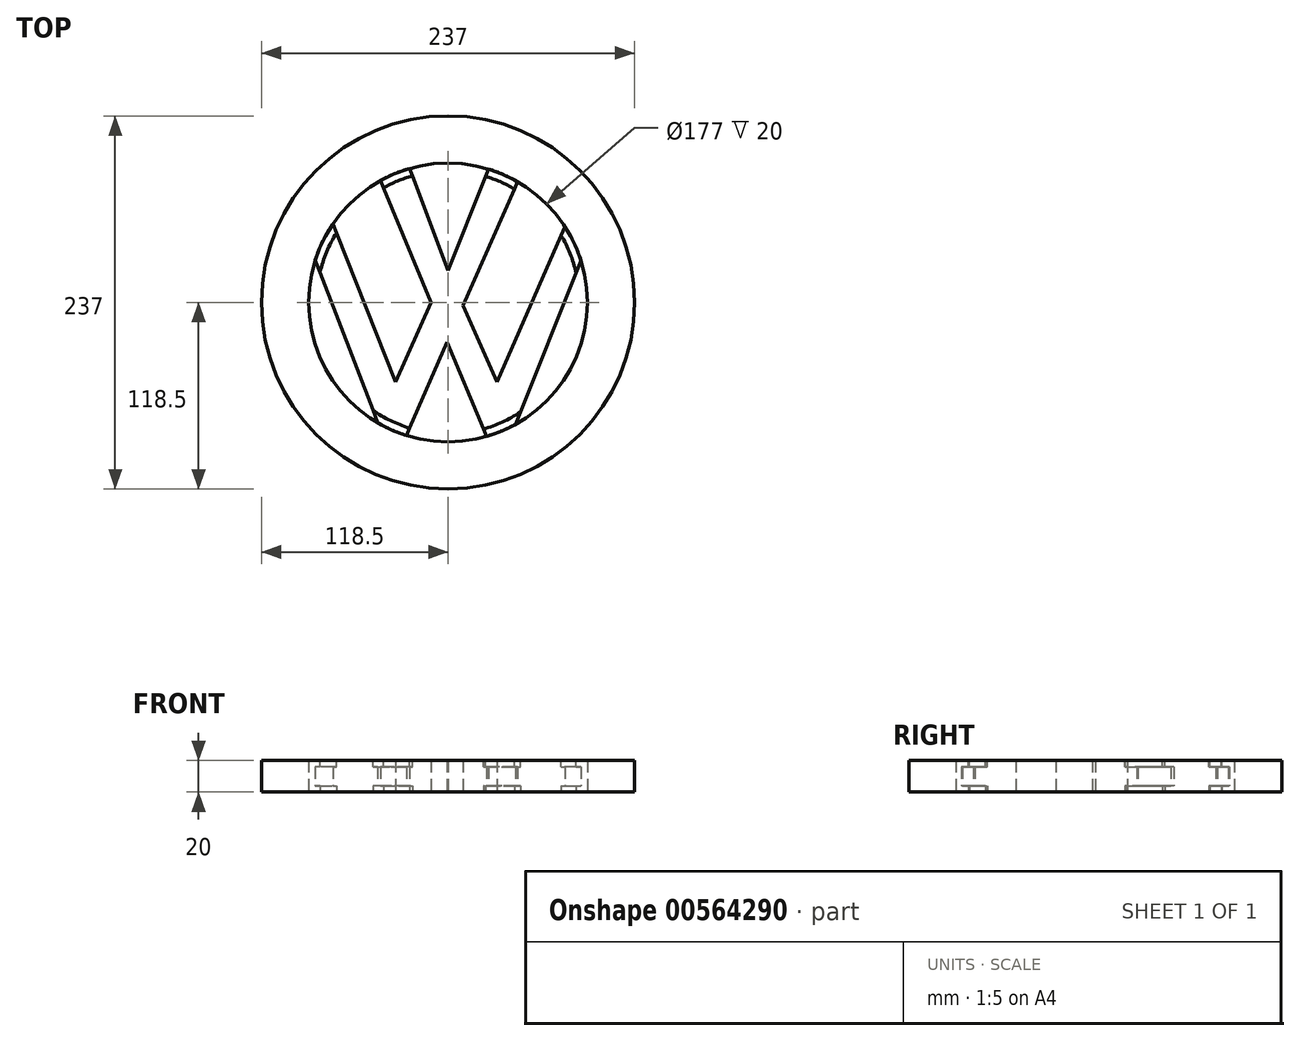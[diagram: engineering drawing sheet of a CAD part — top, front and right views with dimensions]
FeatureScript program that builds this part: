
annotation { "Feature Type Name" : "Feature", "Feature Type Description" : "" }
export const myFeature = defineFeature(function(context is Context, id is Id, definition is map)
    precondition{}
    {
        {
            var Q0;
            Q0=qCreatedBy(makeId("Top.planeOp"),FACE);
            var sketch = newSketch(context, id + "F0", { "sketchPlane" : qUnion([Q0])});
            skCircle(sketch, "E0", {"center": v(0, 0) * mm, "radius": 118.5 * mm});
            skCircle(sketch, "E1", {"center": v(0, 0) * mm, "radius": 88.5 * mm});
            skLineSegment(sketch, "E2", {"start": v(-24.48, 85.05) * mm, "end": v(0, 20.32) * mm});
            skLineSegment(sketch, "E3", {"start": v(0, 20.32) * mm, "end": v(25.75, 84.67) * mm});
            skLineSegment(sketch, "E4", {"start": v(-42.95, 77.38) * mm, "end": v(24.31, -85.1) * mm});
            skLineSegment(sketch, "E5", {"start": v(44.1, 76.73) * mm, "end": v(-26.48, -84.44) * mm});
            skLineSegment(sketch, "E6", {"start": v(-10.91, 0) * mm, "end": v(-44.77, -76.34) * mm});
            skLineSegment(sketch, "E7", {"start": v(8.81, 0) * mm, "end": v(42.8, -77.46) * mm});
            skPoint(sketch, "E7.startSnap0", {"position": v(8.81, -3.86) * mm});
            skLineSegment(sketch, "E8", {"start": v(-44.77, -76.34) * mm, "end": v(-84.3, 26.96) * mm});
            skLineSegment(sketch, "E9", {"start": v(-73.11, 49.87) * mm, "end": v(-33.34, -50.57) * mm});
            skLineSegment(sketch, "E10", {"start": v(42.8, -77.46) * mm, "end": v(84.46, 26.44) * mm});
            skLineSegment(sketch, "E11", {"start": v(31, -50.57) * mm, "end": v(74.25, 48.16) * mm});
            skSolve(sketch);
        }
        {
            var Q0;
            Q0=qSketchRegion(id+"F0",true);
            extrude(context, id + "F1", {"entities" : qUnion([Q0]), "depth" : 20 * mm, "offsetDistance" : 25 * mm});
        }
        {
            var Q0;
            {var subQ0=sQuery(id+"F0.wireOp",EDGE,"E8");Q0=makeQuery(id+"F0.imprint","IMPRINT",FACE,{"disambiguationData":[TD([[makeQuery(id+"F0.imprint","IMPRINT",EDGE,{"derivedFrom":subQ0}),-1.0]])]});}
            var Q1;
            {var subQ3=sQuery(id+"F0.wireOp",EDGE,"E4");var subQ5=sQuery(id+"F0.wireOp",EDGE,"E6");var subQ7=makeQuery(id+"F0.imprint","INTERSECT",VERTEX,{"derivedFrom":[subQ3,subQ5]});Q1=makeQuery(id+"F0.imprint","IMPRINT",FACE,{"disambiguationData":[TD([[makeQuery(id+"F0.imprint","IMPRINT",EDGE,{"disambiguationData":[TD([[subQ7,-1.0]])],"derivedFrom":subQ3}),-1.0]])]});}
            var Q2;
            {var subQ4=sQuery(id+"F0.wireOp",EDGE,"E2");Q2=makeQuery(id+"F0.imprint","IMPRINT",FACE,{"disambiguationData":[TD([[makeQuery(id+"F0.imprint","IMPRINT",EDGE,{"derivedFrom":subQ4}),-1.0]])]});}
            var Q3;
            {var subQ4=sQuery(id+"F0.wireOp",EDGE,"E4");var subQ6=sQuery(id+"F0.wireOp",EDGE,"E1");var subQ7=makeQuery(id+"F0.imprint","INTERSECT",VERTEX,{"disambiguationData":[OD(1.0)],"derivedFrom":[subQ6,subQ4]});Q3=makeQuery(id+"F0.imprint","IMPRINT",FACE,{"disambiguationData":[TD([[makeQuery(id+"F0.imprint","IMPRINT",EDGE,{"disambiguationData":[TD([[subQ7,1.0]])],"derivedFrom":subQ4}),1.0]])]});}
            var Q4;
            {var subQ0=sQuery(id+"F0.wireOp",EDGE,"E10");Q4=makeQuery(id+"F0.imprint","IMPRINT",FACE,{"disambiguationData":[TD([[makeQuery(id+"F0.imprint","IMPRINT",EDGE,{"derivedFrom":subQ0}),1.0]])]});}
            extrude(context, id + "F2", {"entities" : qUnion([Q0, Q1, Q2, Q3, Q4]), "operationType" : NewBodyOperationType.ADD, "depth" : 20 * mm, "offsetDistance" : 25 * mm});
        }
        {
            var Q0;
            {var subQ0=sQuery(id+"F0.wireOp",EDGE,"E1");Q0=makeQuery(id+"F2.boolean.opBoolean","MERGE",FACE,{"derivedFrom":[makeQuery(id+"F1.opExtrude","CAP_FACE",FACE,{"disambiguationData":[OSD([sQuery(id+"F0.wireOp",EDGE,"E0"),subQ0])],"isStart":false}),makeQuery(id+"F2.opExtrude","CAP_FACE",FACE,{"disambiguationData":[OSD([subQ0,sQuery(id+"F0.wireOp",EDGE,"E2"),sQuery(id+"F0.wireOp",EDGE,"E3"),sQuery(id+"F0.wireOp",EDGE,"E4"),sQuery(id+"F0.wireOp",EDGE,"E5"),sQuery(id+"F0.wireOp",EDGE,"E6"),sQuery(id+"F0.wireOp",EDGE,"E7"),sQuery(id+"F0.wireOp",EDGE,"E8"),sQuery(id+"F0.wireOp",EDGE,"E9"),sQuery(id+"F0.wireOp",EDGE,"E10"),sQuery(id+"F0.wireOp",EDGE,"E11")])],"isStart":false})]});}
            var sketch = newSketch(context, id + "F3", { "sketchPlane" : qUnion([Q0])});
            skCircle(sketch, "E12", {"center": v(0, 0) * mm, "radius": 88.5 * mm});
            skCircle(sketch, "E13", {"center": v(0, 0) * mm, "radius": 83.5 * mm});
            skLineSegment(sketch, "E14.bottom", {"start": v(-12.16, 3) * mm, "end": v(10.13, 3) * mm});
            skLineSegment(sketch, "E14.top", {"start": v(-12.16, -3) * mm, "end": v(10.13, -3) * mm});
            skLineSegment(sketch, "E14.left", {"start": v(-12.16, 3) * mm, "end": v(-12.16, -3) * mm});
            skLineSegment(sketch, "E14.right", {"start": v(10.13, 3) * mm, "end": v(10.13, -3) * mm});
            skSolve(sketch);
        }
        {
            var Q0;
            {var subQ0=sQuery(id+"F3.wireOp",EDGE,"E12");var subQ4=makeQuery(id+"F2.opExtrude","CAP_EDGE",EDGE,{"disambiguationData":[OSD([sQuery(id+"F0.wireOp",EDGE,"E10")])],"isStart":false});var subQ5=makeQuery(id+"F3.imprint","INTERSECT",VERTEX,{"disambiguationData":[OD(0.0)],"derivedFrom":[subQ4,subQ0]});Q0=makeQuery(id+"F3.imprint","IMPRINT",FACE,{"disambiguationData":[TD([[makeQuery(id+"F3.imprint","IMPRINT",EDGE,{"disambiguationData":[TD([[subQ5,-1.0]])],"derivedFrom":subQ4}),1.0]])]});}
            var Q1;
            {var subQ0=sQuery(id+"F3.wireOp",EDGE,"E12");var subQ4=makeQuery(id+"F2.opExtrude","CAP_EDGE",EDGE,{"disambiguationData":[OSD([sQuery(id+"F0.wireOp",EDGE,"E8")])],"isStart":false});var subQ5=makeQuery(id+"F3.imprint","INTERSECT",VERTEX,{"disambiguationData":[OD(0.0)],"derivedFrom":[subQ4,subQ0]});Q1=makeQuery(id+"F3.imprint","IMPRINT",FACE,{"disambiguationData":[TD([[makeQuery(id+"F3.imprint","IMPRINT",EDGE,{"disambiguationData":[TD([[subQ5,-1.0]])],"derivedFrom":subQ4}),-1.0]])]});}
            var Q2;
            {var subQ0=sQuery(id+"F3.wireOp",EDGE,"E12");var subQ1=makeQuery(id+"F2.opExtrude","CAP_EDGE",EDGE,{"disambiguationData":[OSD([sQuery(id+"F0.wireOp",EDGE,"E8")])],"isStart":false});var subQ2=makeQuery(id+"F3.imprint","INTERSECT",VERTEX,{"disambiguationData":[OD(1.0)],"derivedFrom":[subQ1,subQ0]});Q2=makeQuery(id+"F3.imprint","IMPRINT",FACE,{"disambiguationData":[TD([[makeQuery(id+"F3.imprint","IMPRINT",EDGE,{"disambiguationData":[TD([[subQ2,1.0]])],"derivedFrom":subQ0}),1.0]])]});}
            var Q3;
            {var subQ0=sQuery(id+"F3.wireOp",EDGE,"E12");var subQ1=makeQuery(id+"F2.opExtrude","CAP_EDGE",EDGE,{"disambiguationData":[OSD([sQuery(id+"F0.wireOp",EDGE,"E2")])],"isStart":false});var subQ2=makeQuery(id+"F3.imprint","INTERSECT",VERTEX,{"derivedFrom":[subQ1,subQ0]});Q3=makeQuery(id+"F3.imprint","IMPRINT",FACE,{"disambiguationData":[TD([[makeQuery(id+"F3.imprint","IMPRINT",EDGE,{"disambiguationData":[TD([[subQ2,-1.0]])],"derivedFrom":subQ1}),-1.0]])]});}
            var Q4;
            {var subQ0=sQuery(id+"F3.wireOp",EDGE,"E12");var subQ1=makeQuery(id+"F2.opExtrude","CAP_EDGE",EDGE,{"disambiguationData":[OSD([sQuery(id+"F0.wireOp",EDGE,"E3")])],"isStart":false});var subQ2=makeQuery(id+"F3.imprint","INTERSECT",VERTEX,{"derivedFrom":[subQ1,subQ0]});Q4=makeQuery(id+"F3.imprint","IMPRINT",FACE,{"disambiguationData":[TD([[makeQuery(id+"F3.imprint","IMPRINT",EDGE,{"disambiguationData":[TD([[subQ2,1.0]])],"derivedFrom":subQ1}),-1.0]])]});}
            var Q5;
            {var subQ0=sQuery(id+"F3.wireOp",EDGE,"E12");var subQ1=makeQuery(id+"F2.opExtrude","CAP_EDGE",EDGE,{"disambiguationData":[OSD([sQuery(id+"F0.wireOp",EDGE,"E10")])],"isStart":false});var subQ2=makeQuery(id+"F3.imprint","INTERSECT",VERTEX,{"disambiguationData":[OD(1.0)],"derivedFrom":[subQ1,subQ0]});Q5=makeQuery(id+"F3.imprint","IMPRINT",FACE,{"disambiguationData":[TD([[makeQuery(id+"F3.imprint","IMPRINT",EDGE,{"disambiguationData":[TD([[subQ2,-1.0]])],"derivedFrom":subQ0}),1.0]])]});}
            extrude(context, id + "F4", {"entities" : qUnion([Q0, Q1, Q2, Q3, Q4, Q5]), "operationType" : NewBodyOperationType.REMOVE, "oppositeDirection" : true, "depth" : 4 * mm, "offsetDistance" : 25 * mm});
        }
        {
            var Q0;
            {var subQ0=sQuery(id+"F0.wireOp",EDGE,"E1");Q0=makeQuery(id+"F2.boolean.opBoolean","MERGE",FACE,{"derivedFrom":[makeQuery(id+"F1.opExtrude","CAP_FACE",FACE,{"disambiguationData":[OSD([sQuery(id+"F0.wireOp",EDGE,"E0"),subQ0])],"isStart":true}),makeQuery(id+"F2.opExtrude","CAP_FACE",FACE,{"disambiguationData":[OSD([subQ0,sQuery(id+"F0.wireOp",EDGE,"E2"),sQuery(id+"F0.wireOp",EDGE,"E3"),sQuery(id+"F0.wireOp",EDGE,"E4"),sQuery(id+"F0.wireOp",EDGE,"E5"),sQuery(id+"F0.wireOp",EDGE,"E6"),sQuery(id+"F0.wireOp",EDGE,"E7"),sQuery(id+"F0.wireOp",EDGE,"E8"),sQuery(id+"F0.wireOp",EDGE,"E9"),sQuery(id+"F0.wireOp",EDGE,"E10"),sQuery(id+"F0.wireOp",EDGE,"E11")])],"isStart":true})]});}
            var sketch = newSketch(context, id + "F5", { "sketchPlane" : qUnion([Q0])});
            skCircle(sketch, "E15", {"center": v(0, 0) * mm, "radius": 88.5 * mm});
            skCircle(sketch, "E16", {"center": v(0, 0) * mm, "radius": 83.5 * mm});
            skSolve(sketch);
        }
        {
            var Q0;
            {var subQ0=sQuery(id+"F5.wireOp",EDGE,"E15");var subQ4=makeQuery(id+"F2.opExtrude","CAP_EDGE",EDGE,{"disambiguationData":[OSD([sQuery(id+"F0.wireOp",EDGE,"E8")])],"isStart":true});var subQ5=makeQuery(id+"F5.imprint","INTERSECT",VERTEX,{"disambiguationData":[OD(0.0)],"derivedFrom":[subQ4,subQ0]});Q0=makeQuery(id+"F5.imprint","IMPRINT",FACE,{"disambiguationData":[TD([[makeQuery(id+"F5.imprint","IMPRINT",EDGE,{"disambiguationData":[TD([[subQ5,-1.0]])],"derivedFrom":subQ4}),1.0]])]});}
            var Q1;
            {var subQ0=sQuery(id+"F5.wireOp",EDGE,"E15");var subQ4=makeQuery(id+"F2.opExtrude","CAP_EDGE",EDGE,{"disambiguationData":[OSD([sQuery(id+"F0.wireOp",EDGE,"E10")])],"isStart":true});var subQ5=makeQuery(id+"F5.imprint","INTERSECT",VERTEX,{"disambiguationData":[OD(0.0)],"derivedFrom":[subQ4,subQ0]});Q1=makeQuery(id+"F5.imprint","IMPRINT",FACE,{"disambiguationData":[TD([[makeQuery(id+"F5.imprint","IMPRINT",EDGE,{"disambiguationData":[TD([[subQ5,-1.0]])],"derivedFrom":subQ4}),-1.0]])]});}
            var Q2;
            {var subQ0=sQuery(id+"F5.wireOp",EDGE,"E15");var subQ1=makeQuery(id+"F2.opExtrude","CAP_EDGE",EDGE,{"disambiguationData":[OSD([sQuery(id+"F0.wireOp",EDGE,"E10")])],"isStart":true});var subQ2=makeQuery(id+"F5.imprint","INTERSECT",VERTEX,{"disambiguationData":[OD(1.0)],"derivedFrom":[subQ1,subQ0]});var subQ3=makeQuery(id+"F2.opExtrude","CAP_EDGE",EDGE,{"disambiguationData":[OSD([sQuery(id+"F0.wireOp",EDGE,"E11")])],"isStart":true});var subQ4=makeQuery(id+"F5.imprint","INTERSECT",VERTEX,{"derivedFrom":[subQ3,subQ0]});Q2=makeQuery(id+"F5.imprint","IMPRINT",FACE,{"disambiguationData":[TD([[makeQuery(id+"F5.imprint","IMPRINT",EDGE,{"disambiguationData":[TD([[subQ2,1.0],[subQ4,-1.0]])],"derivedFrom":subQ0}),1.0]])]});}
            var Q3;
            {var subQ0=sQuery(id+"F5.wireOp",EDGE,"E15");var subQ1=makeQuery(id+"F2.opExtrude","CAP_EDGE",EDGE,{"disambiguationData":[OSD([sQuery(id+"F0.wireOp",EDGE,"E3")])],"isStart":true});var subQ2=makeQuery(id+"F5.imprint","INTERSECT",VERTEX,{"derivedFrom":[subQ1,subQ0]});Q3=makeQuery(id+"F5.imprint","IMPRINT",FACE,{"disambiguationData":[TD([[makeQuery(id+"F5.imprint","IMPRINT",EDGE,{"disambiguationData":[TD([[subQ2,1.0]])],"derivedFrom":subQ1}),1.0]])]});}
            var Q4;
            {var subQ0=sQuery(id+"F5.wireOp",EDGE,"E15");var subQ1=makeQuery(id+"F2.opExtrude","CAP_EDGE",EDGE,{"disambiguationData":[OSD([sQuery(id+"F0.wireOp",EDGE,"E2")])],"isStart":true});var subQ2=makeQuery(id+"F5.imprint","INTERSECT",VERTEX,{"derivedFrom":[subQ1,subQ0]});Q4=makeQuery(id+"F5.imprint","IMPRINT",FACE,{"disambiguationData":[TD([[makeQuery(id+"F5.imprint","IMPRINT",EDGE,{"disambiguationData":[TD([[subQ2,-1.0]])],"derivedFrom":subQ1}),1.0]])]});}
            var Q5;
            {var subQ0=sQuery(id+"F5.wireOp",EDGE,"E15");var subQ1=makeQuery(id+"F2.opExtrude","CAP_EDGE",EDGE,{"disambiguationData":[OSD([sQuery(id+"F0.wireOp",EDGE,"E8")])],"isStart":true});var subQ2=makeQuery(id+"F5.imprint","INTERSECT",VERTEX,{"disambiguationData":[OD(1.0)],"derivedFrom":[subQ1,subQ0]});var subQ3=makeQuery(id+"F2.opExtrude","CAP_EDGE",EDGE,{"disambiguationData":[OSD([sQuery(id+"F0.wireOp",EDGE,"E9")])],"isStart":true});var subQ4=makeQuery(id+"F5.imprint","INTERSECT",VERTEX,{"derivedFrom":[subQ3,subQ0]});Q5=makeQuery(id+"F5.imprint","IMPRINT",FACE,{"disambiguationData":[TD([[makeQuery(id+"F5.imprint","IMPRINT",EDGE,{"disambiguationData":[TD([[subQ2,-1.0],[subQ4,1.0]])],"derivedFrom":subQ0}),1.0]])]});}
            extrude(context, id + "F6", {"entities" : qUnion([Q0, Q1, Q2, Q3, Q4, Q5]), "operationType" : NewBodyOperationType.REMOVE, "oppositeDirection" : true, "depth" : 4 * mm, "offsetDistance" : 25 * mm});
        }
    });
